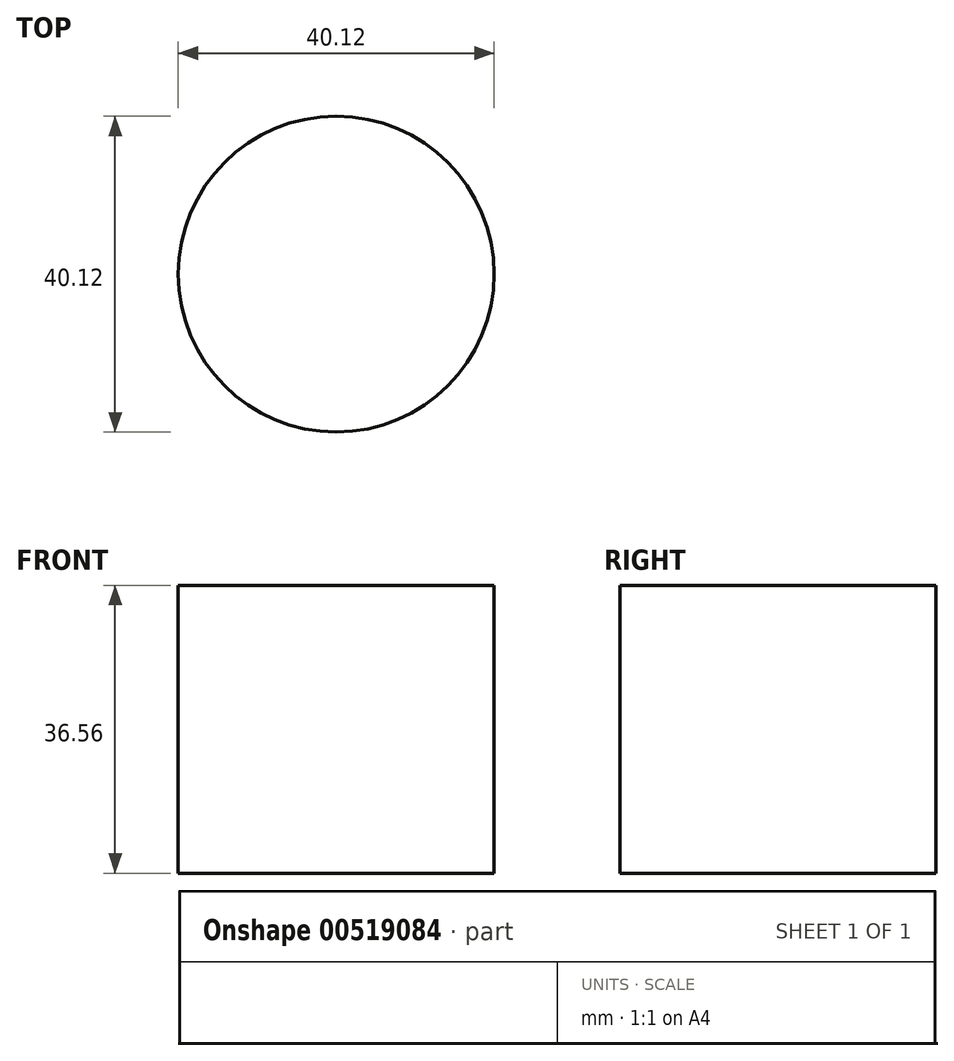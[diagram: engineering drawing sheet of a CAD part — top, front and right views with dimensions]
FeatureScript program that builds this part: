
annotation { "Feature Type Name" : "Feature", "Feature Type Description" : "" }
export const myFeature = defineFeature(function(context is Context, id is Id, definition is map)
    precondition{}
    {
        {
            var Q0;
            Q0=qCreatedBy(makeId("Front.planeOp"),FACE);
            var sketch = newSketch(context, id + "F0", { "sketchPlane" : qUnion([Q0])});
            skLineSegment(sketch, "E0.bottom", {"start": v(0, 36.56) * mm, "end": v(20.06, 36.56) * mm});
            skLineSegment(sketch, "E0.top", {"start": v(0, 0) * mm, "end": v(20.06, 0) * mm});
            skLineSegment(sketch, "E0.left", {"start": v(0, 36.56) * mm, "end": v(0, 0) * mm});
            skLineSegment(sketch, "E0.right", {"start": v(20.06, 36.56) * mm, "end": v(20.06, 0) * mm});
            skSolve(sketch);
        }
        {
            var Q0;
            Q0=makeQuery(id+"F0.imprint","IMPRINT",FACE,{"disambiguationData":[TD([[makeQuery(id+"F0.imprint","IMPRINT",EDGE,{"derivedFrom":sQuery(id+"F0.wireOp",EDGE,"E0.bottom")}),-1.0]])]});
            var Q1;
            Q1=sQuery(id+"F0.wireOp",EDGE,"E0.left");
            revolve(context, id + "F1", {"entities" : qUnion([Q0]), "axis" : qUnion([Q1]), "revolveType" : RevolveType.FULL});
        }
    });
